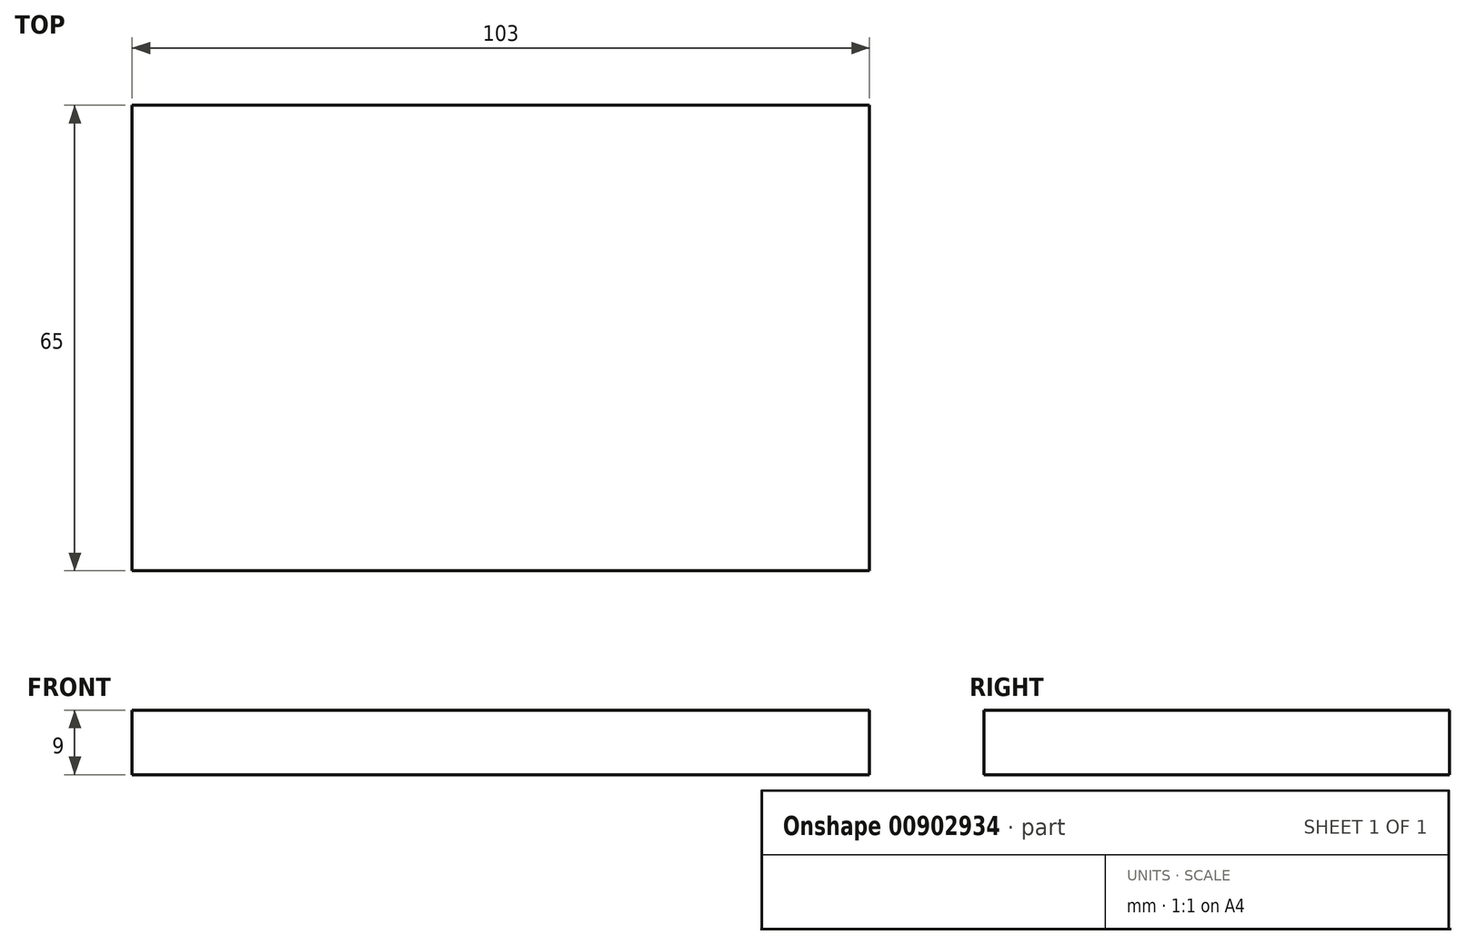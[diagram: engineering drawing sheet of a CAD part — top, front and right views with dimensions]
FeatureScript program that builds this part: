
annotation { "Feature Type Name" : "Feature", "Feature Type Description" : "" }
export const myFeature = defineFeature(function(context is Context, id is Id, definition is map)
    precondition{}
    {
        {
            var Q0;
            Q0=qCreatedBy(makeId("Top.planeOp"),FACE);
            var sketch = newSketch(context, id + "F0", { "sketchPlane" : qUnion([Q0])});
            skLineSegment(sketch, "E0.bottom", {"start": v(-47.94, -60.19) * mm, "end": v(55.06, -60.19) * mm});
            skLineSegment(sketch, "E0.top", {"start": v(-47.94, 4.81) * mm, "end": v(55.06, 4.81) * mm});
            skLineSegment(sketch, "E0.left", {"start": v(-47.94, -60.19) * mm, "end": v(-47.94, 4.81) * mm});
            skLineSegment(sketch, "E0.right", {"start": v(55.06, -60.19) * mm, "end": v(55.06, 4.81) * mm});
            skSolve(sketch);
        }
        {
            var Q0;
            Q0 = qSketchRegion(id + "F0", true);
            extrude(context, id + "F1", {"entities" : qUnion([Q0]), "depth" : 9 * mm, "offsetDistance" : 25 * mm});
        }
    });
